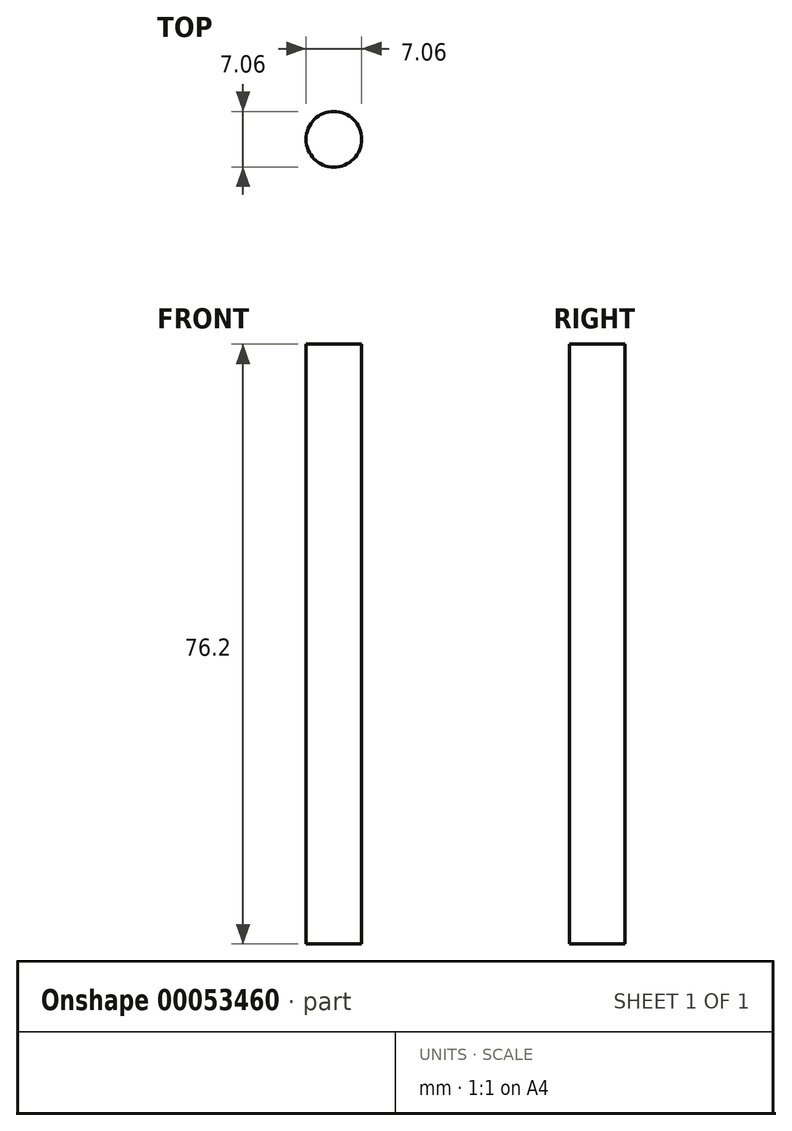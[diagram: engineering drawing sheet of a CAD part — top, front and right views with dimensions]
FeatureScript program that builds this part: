
annotation { "Feature Type Name" : "Feature", "Feature Type Description" : "" }
export const myFeature = defineFeature(function(context is Context, id is Id, definition is map)
    precondition{}
    {
        {
            var Q0;
            Q0=qCreatedBy(makeId("Top.planeOp"),FACE);
            var sketch = newSketch(context, id + "F0", { "sketchPlane" : qUnion([Q0])});
            skCircle(sketch, "E0", {"center": v(0, 0) * mm, "radius": 3.53 * mm});
            skSolve(sketch);
        }
        {
            var Q0;
            Q0=makeQuery(id+"F0.imprint","IMPRINT",FACE,{"disambiguationData":[TD([[makeQuery(id+"F0.imprint","IMPRINT",EDGE,{"derivedFrom":sQuery(id+"F0.wireOp",EDGE,"E0")}),1.0]])]});
            extrude(context, id + "F1", {"entities" : qUnion([Q0]), "depth" : 76.2 * mm});
        }
    });
